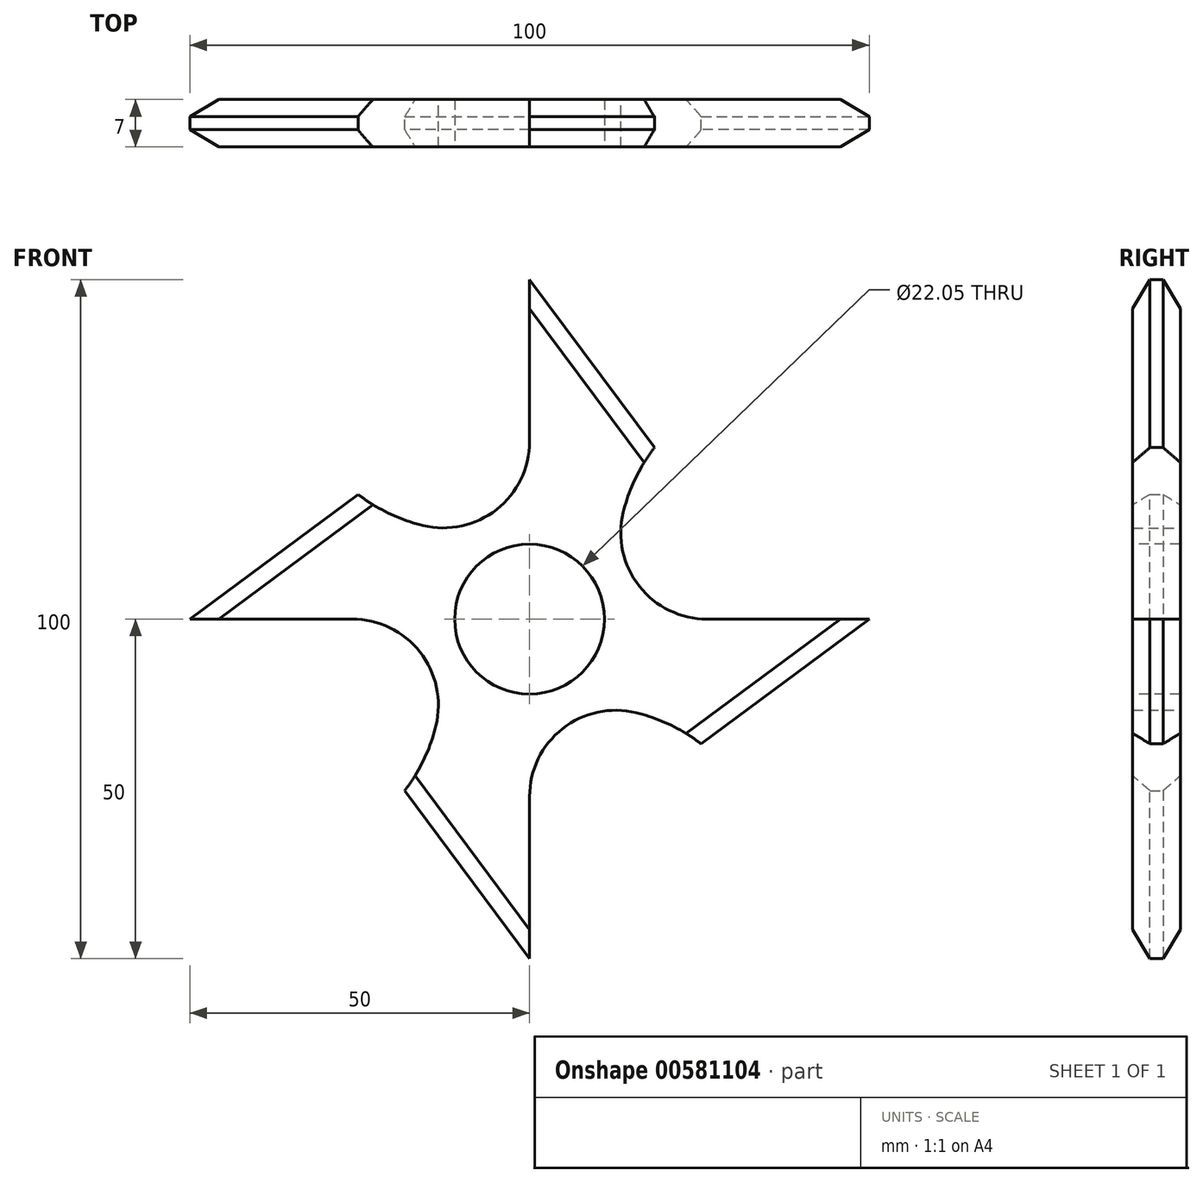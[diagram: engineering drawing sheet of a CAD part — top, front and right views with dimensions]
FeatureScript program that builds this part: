
annotation { "Feature Type Name" : "Feature", "Feature Type Description" : "" }
export const myFeature = defineFeature(function(context is Context, id is Id, definition is map)
    precondition{}
    {
        {
            var Q0;
            Q0=qCreatedBy(makeId("Front.planeOp"),FACE);
            var sketch = newSketch(context, id + "F0", { "sketchPlane" : qUnion([Q0])});
            skLineSegment(sketch, "E0", {"start": v(0, 0) * mm, "end": v(0, 50) * mm});
            skLineSegment(sketch, "E1", {"start": v(0, 0) * mm, "end": v(15, 0) * mm});
            skLineSegment(sketch, "E2", {"start": v(18.38, 25.25) * mm, "end": v(0, 50) * mm});
            skArc(sketch, "E3", {"start": v(18.38, 25.25) * mm, "mid": v(13.3, 13.08) * mm, "end": v(15, 0) * mm});
            skLineSegment(sketch, "E4.1.0", {"start": v(-25.25, 18.38) * mm, "end": v(-50, 0) * mm});
            skLineSegment(sketch, "E4.1.1", {"start": v(0, 0) * mm, "end": v(-50, 0) * mm});
            skArc(sketch, "E4.1.2", {"start": v(-25.25, 18.38) * mm, "mid": v(-13.08, 13.3) * mm, "end": v(0, 15) * mm});
            skLineSegment(sketch, "E4.1.3", {"start": v(0, 0) * mm, "end": v(0, 15) * mm});
            skLineSegment(sketch, "E4.2.0", {"start": v(-18.38, -25.25) * mm, "end": v(0, -50) * mm});
            skLineSegment(sketch, "E4.2.1", {"start": v(0, 0) * mm, "end": v(0, -50) * mm});
            skArc(sketch, "E4.2.2", {"start": v(-18.38, -25.25) * mm, "mid": v(-13.3, -13.08) * mm, "end": v(-15, 0) * mm});
            skLineSegment(sketch, "E4.2.3", {"start": v(0, 0) * mm, "end": v(-15, 0) * mm});
            skLineSegment(sketch, "E4.3.0", {"start": v(25.25, -18.38) * mm, "end": v(50, 0) * mm});
            skLineSegment(sketch, "E4.3.1", {"start": v(0, 0) * mm, "end": v(50, 0) * mm});
            skArc(sketch, "E4.3.2", {"start": v(25.25, -18.38) * mm, "mid": v(13.08, -13.3) * mm, "end": v(0, -15) * mm});
            skLineSegment(sketch, "E4.3.3", {"start": v(0, 0) * mm, "end": v(0, -15) * mm});
            skPoint(sketch, "E4.center", {"position": v(0, 0) * mm});
            skSolve(sketch);
        }
        {
            var Q0;
            Q0=qSketchRegion(id+"F0",true);
            extrude(context, id + "F1", {"entities" : qUnion([Q0]), "depth" : 7 * mm, "offsetDistance" : 25.4 * mm});
        }
        {
            var Q0;
            Q0=makeQuery(id+"F1.opExtrude","CAP_FACE",FACE,{"disambiguationData":[OSD([sQuery(id+"F0.wireOp",EDGE,"E0"),sQuery(id+"F0.wireOp",EDGE,"E2"),sQuery(id+"F0.wireOp",EDGE,"E3"),sQuery(id+"F0.wireOp",EDGE,"E4.1.0"),sQuery(id+"F0.wireOp",EDGE,"E4.1.1"),sQuery(id+"F0.wireOp",EDGE,"E4.1.2"),sQuery(id+"F0.wireOp",EDGE,"E4.2.0"),sQuery(id+"F0.wireOp",EDGE,"E4.2.1"),sQuery(id+"F0.wireOp",EDGE,"E4.2.2"),sQuery(id+"F0.wireOp",EDGE,"E4.3.0"),sQuery(id+"F0.wireOp",EDGE,"E4.3.1"),sQuery(id+"F0.wireOp",EDGE,"E4.3.2")])],"isStart":false});
            var sketch = newSketch(context, id + "F2", { "sketchPlane" : qUnion([Q0])});
            skCircle(sketch, "E5", {"center": v(0, 0) * mm, "radius": 11.03 * mm});
            skSolve(sketch);
        }
        {
            var Q0;
            Q0=qSketchRegion(id+"F2",true);
            extrude(context, id + "F3", {"entities" : qUnion([Q0]), "operationType" : NewBodyOperationType.REMOVE, "oppositeDirection" : true, "depth" : 25.4 * mm, "offsetDistance" : 25.4 * mm});
        }
        {
            var Q0;
            Q0=makeQuery(id+"F1.opExtrude","SWEPT_EDGE",EDGE,{"disambiguationData":[OSD([sQuery(id+"F0.wireOp",EDGE,"E0"),sQuery(id+"F0.wireOp",EDGE,"E4.1.2"),sQuery(id+"F0.wireOp",EDGE,"E4.1.3")])]});
            var Q1;
            Q1=makeQuery(id+"F1.opExtrude","SWEPT_EDGE",EDGE,{"disambiguationData":[OSD([sQuery(id+"F0.wireOp",EDGE,"E3"),sQuery(id+"F0.wireOp",EDGE,"E4.3.1")])]});
            var Q2;
            Q2=makeQuery(id+"F1.opExtrude","SWEPT_EDGE",EDGE,{"disambiguationData":[OSD([sQuery(id+"F0.wireOp",EDGE,"E4.2.1"),sQuery(id+"F0.wireOp",EDGE,"E4.3.2"),sQuery(id+"F0.wireOp",EDGE,"E4.3.3")])]});
            var Q3;
            Q3=makeQuery(id+"F1.opExtrude","SWEPT_EDGE",EDGE,{"disambiguationData":[OSD([sQuery(id+"F0.wireOp",EDGE,"E4.1.1"),sQuery(id+"F0.wireOp",EDGE,"E4.2.2"),sQuery(id+"F0.wireOp",EDGE,"E4.2.3")])]});
            fillet(context, id + "F4", {"entities" : qUnion([Q0, Q1, Q2, Q3]), "radius" : 12.7 * mm, "tangentPropagation" : true, "allowEdgeOverflow" : false});
        }
        {
            var Q0;
            Q0=makeQuery(id+"F1.opExtrude","CAP_EDGE",EDGE,{"disambiguationData":[OSD([sQuery(id+"F0.wireOp",EDGE,"E4.3.0")])],"isStart":true});
            var Q1;
            Q1=makeQuery(id+"F1.opExtrude","CAP_EDGE",EDGE,{"disambiguationData":[OSD([sQuery(id+"F0.wireOp",EDGE,"E4.3.0")])],"isStart":false});
            var Q2;
            Q2=makeQuery(id+"F1.opExtrude","CAP_EDGE",EDGE,{"disambiguationData":[OSD([sQuery(id+"F0.wireOp",EDGE,"E2")])],"isStart":true});
            var Q3;
            Q3=makeQuery(id+"F1.opExtrude","CAP_EDGE",EDGE,{"disambiguationData":[OSD([sQuery(id+"F0.wireOp",EDGE,"E2")])],"isStart":false});
            var Q4;
            Q4=makeQuery(id+"F1.opExtrude","CAP_EDGE",EDGE,{"disambiguationData":[OSD([sQuery(id+"F0.wireOp",EDGE,"E4.2.0")])],"isStart":true});
            var Q5;
            Q5=makeQuery(id+"F1.opExtrude","CAP_EDGE",EDGE,{"disambiguationData":[OSD([sQuery(id+"F0.wireOp",EDGE,"E4.2.0")])],"isStart":false});
            var Q6;
            Q6=makeQuery(id+"F1.opExtrude","CAP_EDGE",EDGE,{"disambiguationData":[OSD([sQuery(id+"F0.wireOp",EDGE,"E4.1.0")])],"isStart":true});
            var Q7;
            Q7=makeQuery(id+"F1.opExtrude","CAP_EDGE",EDGE,{"disambiguationData":[OSD([sQuery(id+"F0.wireOp",EDGE,"E4.1.0")])],"isStart":false});
            chamfer(context, id + "F5", {"entities" : qUnion([Q0, Q1, Q2, Q3, Q4, Q5, Q6, Q7]), "width" : 2.54 * mm, "tangentPropagation" : true});
        }
    });
